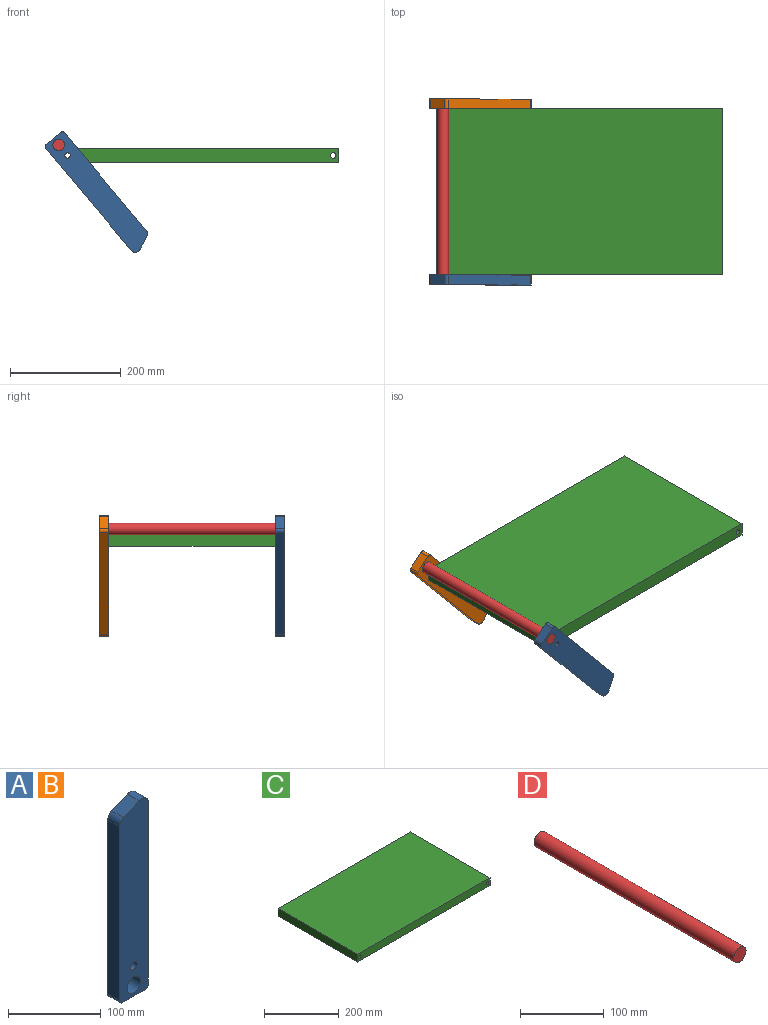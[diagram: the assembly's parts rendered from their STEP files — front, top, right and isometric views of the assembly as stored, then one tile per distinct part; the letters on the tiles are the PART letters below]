
ASSEMBLY  parts=4 mates=7
PART A: 12 faces, bbox 44x18x254.9 mm
  f0: plane 254.89x44mm, normal (0,1,0), area 10533.3mm2, adj f2,f3,f4,f5,f6,f7,f8,f9
  f1: plane 254.89x44mm, normal (0,-1,0), area 10533.3mm2, adj f2,f3,f4,f5,f6,f7,f8,f9
  f2: plane 229.7x18mm, normal (-1,0,0), area 4134.7mm2, adj f0,f1,f7,f10
  f3: plane 239.89x18mm, normal (1,0,0), area 4318mm2, adj f0,f1,f8,f11
  f4: plane 34x18mm, normal (0,0,-1), area 612mm2, adj f0,f1,f7,f8
  f5: cylinder r=10.5mm len=21mm, axis (0,-1,0), area 1187.5mm2, adj f0,f1
  f6: cylinder r=5mm len=18mm, axis (0,-1,0), area 565.5mm2, adj f0,f1
  f7: cylinder r=5mm len=18mm, axis (0,-1,0), area 141.4mm2, adj f0,f1,f2,f4
  f8: cylinder r=5mm len=18mm, axis (0,1,0), area 141.4mm2, adj f0,f1,f3,f4
  f9: plane 24x18mm, normal (-0.39,0,0.92), area 469.3mm2, adj f0,f1,f10,f11
  f10: cylinder r=10mm len=18mm, axis (0,-1,0), area 210.5mm2, adj f0,f1,f2,f9
  f11: cylinder r=10mm len=18mm, axis (0,-1,0), area 355mm2, adj f0,f1,f3,f9
PART B: same geometry as A
PART C: 8 faces, bbox 500x300x25 mm
  f0: plane 500x25mm, normal (0,1,0), area 12342.9mm2, adj f2,f3,f4,f5,f6,f7
  f1: plane 500x25mm, normal (0,-1,0), area 12342.9mm2, adj f2,f3,f4,f5,f6,f7
  f2: plane 300x25mm, normal (-1,0,0), area 7500mm2, adj f0,f1,f4,f5
  f3: plane 300x25mm, normal (1,0,0), area 7500mm2, adj f0,f1,f4,f5
  f4: plane 500x300mm, normal (0,0,1), area 150000mm2, adj f0,f1,f2,f3
  f5: plane 500x300mm, normal (0,0,-1), area 150000mm2, adj f0,f1,f2,f3
  f6: cylinder r=5mm len=300mm, axis (0,-1,0), area 9424.8mm2, adj f0,f1
  f7: cylinder r=5mm len=300mm, axis (0,-1,0), area 9424.8mm2, adj f0,f1
PART D: 3 faces, bbox 21x336x21 mm
  f0: cylinder r=10.5mm len=336mm, axis (0,-1,0), area 22167.1mm2, adj f1,f2
  f1: plane 21x21mm, normal (0,1,0), area 346.4mm2, adj f0
  f2: plane 21x21mm, normal (0,-1,0), area 346.4mm2, adj f0
PLACE A rot(axis=(0,1,0),140.1deg) t=(-265.68,-159,43.17)mm
PLACE B rot(axis=(0,1,0),140.1deg) t=(-265.68,159,43.17)mm
PLACE C at identity
PLACE D t=(-256.05,-168,31.67)mm
MATE cylindrical B.f5 <-> D.f0  axis (0,1,0) through (-256.05,168,31.67)mm
MATE planar B.f0 <-> D.f0  axis (0,1,0) through (-182.98,168,-55.91)mm
MATE planar D.f0 <-> A.f1  axis (0,-1,0) through (-256.05,-168,31.67)mm
MATE cylindrical A.f5 <-> D.f0  axis (0,-1,0) through (-256.05,-168,31.67)mm
MATE planar A.f3 <-> B.f3  axis (-0.77,0,-0.64) through (-202.33,-159,-66.75)mm
MATE planar A.f0 <-> C.f1  axis (0,1,0) through (-182.98,-150,-55.91)mm
MATE cylindrical A.f6 <-> C.f6  axis (0,1,0) through (-240,-150,12.5)mm
